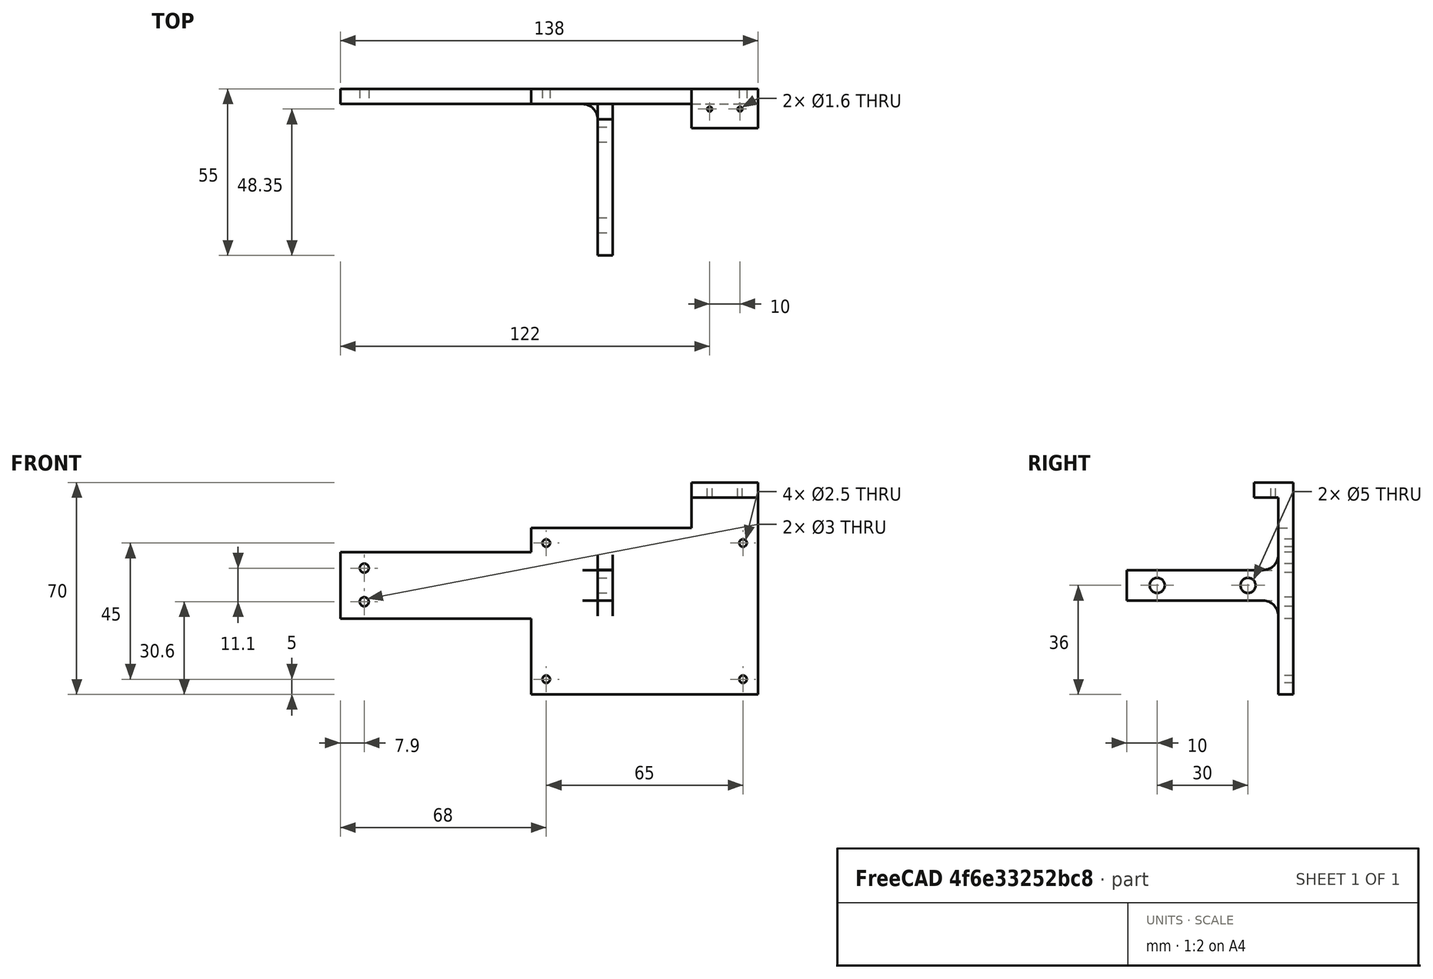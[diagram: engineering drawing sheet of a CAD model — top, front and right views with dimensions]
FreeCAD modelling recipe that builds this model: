
FCSTD DOCUMENT  (FreeCAD 0.18R16110 (Git))
Label: control-board-mount
License: All rights reserved
LicenseURL: http://en.wikipedia.org/wiki/All_rights_reserved
objects: Part::Cut×14, Part::Cylinder×12, Part::Box×5, Part::MultiFuse×2, Spreadsheet::Sheet×1, Mesh::Feature×1
note: 33 computed .brp shape members not serialized (recipe doc carries the construction recipe); baked Part::Feature solids carry a one-line shape summary decoded from their .brp

FEATURE [Part::Box] Box065  label="Quader044"
  AttacherType = Attacher::AttachEngine3D
  Height = 5
  Length = 22
  Placement = pos=(26,-29.35,4) rot=(0,0,1;0rad)
  Width = 10
  expr: Placement.Base.y = -Spreadsheet.E27 - Spreadsheet.E24 / 2 + 25 - 8
FEATURE [Part::Cylinder] Cylinder092  label="Zylinder080"
  Angle = 90
  AttacherType = Attacher::AttachEngine3D
  Height = 5
  Placement = pos=(-5,-26.35,-15) rot=(0,1,0;1.5708rad)
  Radius = 8
  expr: Placement.Base.z = -25 + 5 + 5
  expr: Placement.Base.y = -Spreadsheet.E27 - Spreadsheet.E24 / 2 + 25 - 5
FEATURE [Part::Cylinder] Cylinder094  label="Zylinder082"
  Angle = 360
  AttacherType = Attacher::AttachEngine3D
  Height = 10
  Placement = pos=(-82.1,-13,-19.3) rot=(1,0,0;1.5708rad)
  Radius = 1.5
FEATURE [Part::Box] Box062  label="Quader041"
  AttacherType = Attacher::AttachEngine3D
  Height = 10
  Length = 5
  Placement = pos=(-5,-71.35,-30) rot=(0,0,1;0rad)
  Width = 50
  expr: Placement.Base.y = -Spreadsheet.E27 - Spreadsheet.E24 / 2 + 15 - (50 - 10)
FEATURE [Part::Cylinder] Cylinder095  label="Zylinder083"
  Angle = 360
  AttacherType = Attacher::AttachEngine3D
  Height = 10
  Placement = pos=(-82.1,-13,-30.4) rot=(1,0,0;1.5708rad)
  Radius = 1.5
FEATURE [Part::Cylinder] Cylinder100  label="Zylinder088"
  Angle = 360
  AttacherType = Attacher::AttachEngine3D
  Height = 10
  Placement = pos=(-22,-14.35,-56) rot=(1,0,0;1.5708rad)
  Radius = 1.25
  expr: Placement.Base.z = -61 + 5
  expr: Placement.Base.x = -27 + 5
FEATURE [Part::Box] Box064  label="Quader043"
  AttacherType = Attacher::AttachEngine3D
  Height = 15
  Length = 22
  Placement = pos=(26,-21.35,-6) rot=(0,0,1;0rad)
  Width = 5
  expr: Placement.Base.y = -Spreadsheet.E27 - Spreadsheet.E24 / 2 + 25
FEATURE [Part::Box] Box061  label="Quader040"
  AttacherType = Attacher::AttachEngine3D
  Height = 22
  Length = 90
  Placement = pos=(-90,-21.35,-36) rot=(0,0,1;0rad)
  Width = 5
  expr: Placement.Base.y = -Spreadsheet.E27 - Spreadsheet.E24 / 2 + 25
FEATURE [Part::Cylinder] Cylinder090  label="Zylinder078"
  Angle = 360
  AttacherType = Attacher::AttachEngine3D
  Height = 5
  Placement = pos=(-5,-31.35,-25) rot=(0,1,0;1.5708rad)
  Radius = 2.5
  expr: Radius = 2.5
  expr: Placement.Base.y = -Spreadsheet.E27 - Spreadsheet.E24 / 2 + 15
FEATURE [Part::Cylinder] Cylinder089  label="Zylinder077"
  Angle = 360
  AttacherType = Attacher::AttachEngine3D
  Height = 5
  Placement = pos=(-5,-61.35,-25) rot=(0,1,0;1.5708rad)
  Radius = 2.5
  expr: Radius = 2.5
  expr: Placement.Base.y = -Spreadsheet.E27 - Spreadsheet.E24 / 2 - 15
FEATURE [Part::Cylinder] Cylinder097  label="Zylinder085"
  Angle = 360
  AttacherType = Attacher::AttachEngine3D
  Height = 7
  Placement = pos=(42,-23,3) rot=(0,0,1;0rad)
  Radius = 0.8
FEATURE [Part::Cylinder] Cylinder098  label="Zylinder086"
  Angle = 360
  AttacherType = Attacher::AttachEngine3D
  Height = 7
  Placement = pos=(32,-23,3) rot=(0,0,1;0rad)
  Radius = 0.8
FEATURE [Part::Cylinder] Cylinder101  label="Zylinder089"
  Angle = 360
  AttacherType = Attacher::AttachEngine3D
  Height = 10
  Placement = pos=(43,-14.35,-11) rot=(1,0,0;1.5708rad)
  Radius = 1.25
  expr: Placement.Base.z = -61 + 5 + 45
  expr: Placement.Base.x = -27 + 5 + 65
FEATURE [Part::Cylinder] Cylinder091  label="Zylinder079"
  Angle = 360
  AttacherType = Attacher::AttachEngine3D
  Height = 10
  Placement = pos=(-5,-26.35,-15) rot=(0,1,0;1.5708rad)
  Radius = 5
  expr: Placement.Base.z = -25 + 5 + 5
  expr: Placement.Base.y = -Spreadsheet.E27 - Spreadsheet.E24 / 2 + 25 - 5
FEATURE [Part::Cut] Cut104
  Base = -> Cylinder092
  Placement = pos=(0,-41.35,-8.7) rot=(1,0,0;1.5708rad)
  Tool = -> Cylinder091
FEATURE [Part::Cut] Cut103
  Base = -> Cylinder092
  Placement = pos=(0,0,0.1) rot=(0,0,1;0rad)
  Tool = -> Cylinder091
FEATURE [Part::Box] Box063  label="Quader042"
  AttacherType = Attacher::AttachEngine3D
  Height = 55
  Length = 75
  Placement = pos=(-27,-21.35,-61) rot=(0,0,1;0rad)
  Width = 5
  expr: Placement.Base.y = -Spreadsheet.E27 - Spreadsheet.E24 / 2 + 25
FEATURE [Part::Cut] Cut105
  Base = -> Cylinder092
  Placement = pos=(-25,0,-25) rot=(0,-1,0;1.5708rad)
  Tool = -> Cylinder091
FEATURE [Part::Cut] Cut114
  Base = -> Cylinder092
  Placement = pos=(-25,0,-20) rot=(0,-1,0;1.5708rad)
  Tool = -> Cylinder091
FEATURE [Part::MultiFuse] Fusion050
  Shapes = -> [Box063,Box061,Box062,Cut103,Cut104,Cut105,Box064,Box065]
FEATURE [Part::Cut] Cut108
  Base = -> Fusion050
  Tool = -> Cylinder089
FEATURE [Part::Cut] Cut109
  Base = -> Cut108
  Tool = -> Cylinder090
FEATURE [Part::Cut] Cut110
  Base = -> Cut109
  Tool = -> Cylinder094
FEATURE [Part::Cut] Cut111
  Base = -> Cut110
  Tool = -> Cylinder095
FEATURE [Part::Cut] Cut112
  Base = -> Cut111
  Tool = -> Cylinder097
FEATURE [Part::Cut] Cut113
  Base = -> Cut112
  Tool = -> Cylinder098
FEATURE [Part::MultiFuse] Fusion051
  Shapes = -> [Cut113,Cut114]
FEATURE [Part::Cut] Cut115
  Base = -> Fusion051
  Tool = -> Cylinder100
FEATURE [Part::Cut] Cut116
  Base = -> Cut115
  Tool = -> Cylinder101
FEATURE [Part::Cylinder] Cylinder102  label="Zylinder090"
  Angle = 360
  AttacherType = Attacher::AttachEngine3D
  Height = 10
  Placement = pos=(43,-14.35,-56) rot=(1,0,0;1.5708rad)
  Radius = 1.25
  expr: Placement.Base.z = -61 + 5
  expr: Placement.Base.x = -27 + 5 + 65
FEATURE [Part::Cut] Cut117
  Base = -> Cut116
  Tool = -> Cylinder102
FEATURE [Part::Cylinder] Cylinder103  label="Zylinder091"
  Angle = 360
  AttacherType = Attacher::AttachEngine3D
  Height = 10
  Placement = pos=(-22,-14.35,-11) rot=(1,0,0;1.5708rad)
  Radius = 1.25
  expr: Placement.Base.z = -61 + 5 + 45
  expr: Placement.Base.x = -27 + 5
FEATURE [Part::Cut] Cut118  label="Contriol-board-mount"
  Base = -> Cut117
  Tool = -> Cylinder103
FEATURE [Spreadsheet::Sheet] Spreadsheet
  cells = A1=Toleranz; B1(tolerance)=0.2; D1=x_pos; E1=0; G1=y_pos; H1=0; A2=z_pos; B2=-10; E2=min 0 / max 297; G2=min y_pos; H2=94; I2=max 560; A3=Z-Support; D3=X-Support; G3=y-Support; J3=structure; A4=Führung d; B4(z_df)=8; D4=Führung d; E4(x_df)=10; G4=Führung d; H4(y_df)=10; J4=profil B; K4=20; A5=Führung l; B5(z_fl)==Spreadsheet.z_hub + Spreadsheet.z_hmount * 2 + Spreadsheet.z_hs - 5; D5=Führung l; E5(x_lf)=420; F5=400; G5=Führung l; H5(y_fl)=700; I5=500; J5=distanz Führung; K5=3; A6=Abstand Führung z_sfa; B6(z_sfa)==(z_dlinear + 2 * z_swand + 2 * z_sriemenspiel + z_lriemen) * 1 + (2 * x_hlinear + +z_swand - z_df + 4 * tolerance) * 0; D6=Abstand Führung x_sfa; E6(x_sfa)=65; G6=Abstand Fü y_sfa; H6(y_sfa)==x_lf - x_dlinear - 2 * y_swand; J6=höhe; K6=300; J7=add to Top; K7=18; A8=Schlittenwand swand; B8(z_swand)=5; D8=Schlitten swand; E8(x_swand)=4; G8=y_swand; H8(y_swand)=5; A9=Schlittenlänge z_ls; B9(z_ls)==z_sfa + z_dlinear; D9=Schlittenlänge; E9(x_ls)==z_lmount; A10=Schlittenbreite z_bs; B10(z_bs)==2 * z_swand + z_dlinear; D10=Schlitten breite; E10(x_bs)==Spreadsheet.x_swand * 2 + Spreadsheet.x_dlinear + Spreadsheet.x_sfa; G10=d Antrieb; H10=5; A11=Schlittenhöhe z_hs; B11(z_hs)==z_hlinear + 2 * z_swand; D11=schlittenhöhe x_hs; E11(x_hs)==x_dlinear + x_swand; A12=Hub; B12(z_hub)=100; A14=Linearlager; A15=durchmesser z_dlinear; B15(z_dlinear)=15.4; D15=durchmesser x_dlinear; E15(x_dlinear)=19.5; A16=höhe z_hlinear; B16(z_hlinear)=24.4; D16=höhe x_hlinear; E16(x_hlinear)=29.4; A18=Riemenscheibe bohrung; B18=5; A19=durchmesser z_driemen; B19(z_driemen)=16; D19=dopper pulley; E19=27.5; F19=15.8; A20=länge z_lriemen; B20(z_lriemen)=28; D20=pulley; E20=15.25; F20=15.8; G20=20 Zähne: 2* 180 °; H20=2mm*20 Zähne; I20==40mm; A21=spiel riemenscheibe z_sriemenspiel; B21(z_sriemenspiel)=2; A22=Bohreung z_dbohrung; B22(z_dbohrung)=8; C22=durchmesser Laufbuchse; D22=x_mount; A23=Bohrunlänge z_lbohrung; B23(z_lbohrung)=5; D23=Breite x_mount; E23==y_swand + x_dlinear; A24=riemenbreite z_briemen; B24(z_briemen)=6; D24=Länge x_mount; E24==x_sfa + x_df + y_swand * 2; A25=pitch z_rriemenpitch; B25(z_rriemepitch)=7; D25=Höhe x_mount; E25==y_swand * 2 + x_df + +y_swand + x_dlinear + y_swand; A26=achsen pos y; B26==-Spreadsheet.z_driemen / 2 - Spreadsheet.tolerance * 2; D26= xpos; E26==-Spreadsheet.E23; A27=achsen pos z; B27==(Spreadsheet.z_hub + Spreadsheet.z_hs + Spreadsheet.x_hs) / 2 + z_hmount - z_dbohrung / 2 - Spreadsheet.z_dbohrung / 2; D27=ypos; E27==Spreadsheet.x_swand + Spreadsheet.x_dlinear / 2 + Spreadsheet.tolerance / 2 - Spreadsheet.x_df / 2 - Spreadsheet.y_swand; D28= zpos; E28==-y_swand; A29=Mount; A30=Höhe mount; B30(z_hmount)=20; A31=Länge mount; B31(z_lmount)==z_swand * 2 + z_df + z_sfa; A32=Breite mount; B32(z_bmount)==(Spreadsheet.z_swand + Spreadsheet.z_driemen + Spreadsheet.tolerance * 2) * 0 + 26; A34=Nema; D34=Nema x; A35=Länge; B35(lnema)=42; D35(nema_x_b)=42; A36=Breite; B36(bnema)=42; D36=42; A37=Höhe; B37(hnema)=34; D37(nema_x_h)=48; A38=Achslänge; B38(lanema)=20; D38(nema_x_al)=22; A39=achsen pos y; B39(nema_achse_y)==sqrt(B43 ^ 2 - (B27 - B40) ^ 2) + B26; E39(nemax_achsey)==Spreadsheet.x_swand + Spreadsheet.x_df / 2 + Spreadsheet.x_dlinear / 2 + Spreadsheet.nema_x_h + 2; A40=achsen pos z; B40(nema_achse_z)==x_hs + lnema / 2 + 4; E40(nema_x_achsez)==-Spreadsheet.x_hs / 2; A41=achsen pos x; B41(nema_achse_x)==(z_lmount - z_lriemen) / 2 - z_sriemenspiel; E41(nema_x_achsex)==Spreadsheet.x_lf - Spreadsheet.nema_x_b / 2 - Spreadsheet.y_df; A42=länge zahnriemen; B42=200; C42=gerechnet; A43=abstand achsen; B43==(B42 - 40) / 2; C43==sqrt((Spreadsheet.B27 - Spreadsheet.nema_achse_z) ^ 2 + (-Spreadsheet.B26 + Spreadsheet.nema_achse_y) ^ 2) * 2 + 2 * pi * 7; D43=Zahnriemen x; D44=Breite; E44=6; A45=doppel pulley; D45=Höhe; E45==(Spreadsheet.F20 + Spreadsheet.tolerance * 2) * 0 + 15; A46= achse1  x pos; B46==z_lmount / 2 - (6.5 + 8.9) / 2; D46=Länge; E46==y_sfa + x_dlinear + y_swand * 2 + 2 + nema_x_b / 2; A47= achse2 xpos; B47==z_lmount / 2 + (6.5 + 8.9) / 2; B48==-atan((Spreadsheet.B27 - Spreadsheet.nema_achse_z) / (-Spreadsheet.B26 + Spreadsheet.nema_achse_y))
FEATURE [Mesh::Feature] Mesh  label="Contriol-board-mount (Meshed)"
